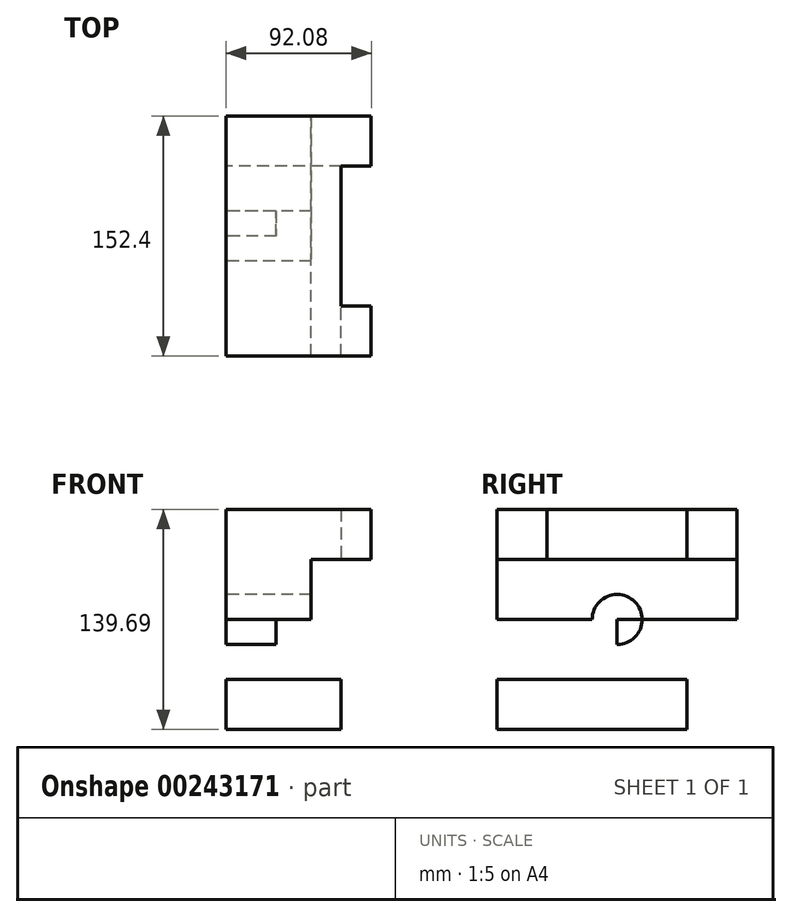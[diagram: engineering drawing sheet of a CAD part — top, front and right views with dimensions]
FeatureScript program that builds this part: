
annotation { "Feature Type Name" : "Feature", "Feature Type Description" : "" }
export const myFeature = defineFeature(function(context is Context, id is Id, definition is map)
    precondition{}
    {
        {
            var Q0;
            Q0=qCreatedBy(makeId("Right.planeOp"),FACE);
            var sketch = newSketch(context, id + "F0", { "sketchPlane" : qUnion([Q0])});
            skLineSegment(sketch, "E0.bottom", {"start": v(-76.2, 85.72) * mm, "end": v(0, 85.72) * mm});
            skLineSegment(sketch, "E0.top", {"start": v(-76.2, -41.28) * mm, "end": v(0, -41.28) * mm});
            skLineSegment(sketch, "E0.left", {"start": v(-76.2, 85.72) * mm, "end": v(-76.2, -41.28) * mm});
            skLineSegment(sketch, "E0.right", {"start": v(0, 85.72) * mm, "end": v(0, -41.28) * mm});
            skLineSegment(sketch, "E1.top", {"start": v(0, 0) * mm, "end": v(-25.4, 0) * mm});
            skLineSegment(sketch, "E1.left", {"start": v(0, -41.28) * mm, "end": v(0, 0) * mm});
            skLineSegment(sketch, "E1.right", {"start": v(-25.4, -41.28) * mm, "end": v(-25.4, 0) * mm});
            skLineSegment(sketch, "E2.top", {"start": v(-76.2, 15.87) * mm, "end": v(0, 15.87) * mm});
            skLineSegment(sketch, "E2.left", {"start": v(-76.2, 85.72) * mm, "end": v(-76.2, 15.87) * mm});
            skLineSegment(sketch, "E2.right", {"start": v(0, 85.72) * mm, "end": v(0, 15.87) * mm});
            skLineSegment(sketch, "E3.top", {"start": v(-76.2, 47.62) * mm, "end": v(0, 47.62) * mm});
            skLineSegment(sketch, "E3.left", {"start": v(-76.2, 85.72) * mm, "end": v(-76.2, 47.62) * mm});
            skLineSegment(sketch, "E3.right", {"start": v(0, 85.72) * mm, "end": v(0, 47.62) * mm});
            skLineSegment(sketch, "E4.left", {"start": v(-76.2, 47.62) * mm, "end": v(-76.2, 15.87) * mm});
            skLineSegment(sketch, "E4.right", {"start": v(0, 47.62) * mm, "end": v(0, 15.87) * mm});
            skLineSegment(sketch, "E5.bottom", {"start": v(-76.2, 47.62) * mm, "end": v(-44.45, 47.62) * mm});
            skLineSegment(sketch, "E5.top", {"start": v(-76.2, 15.87) * mm, "end": v(-44.45, 15.87) * mm});
            skLineSegment(sketch, "E5.right", {"start": v(-44.45, 47.62) * mm, "end": v(-44.45, 15.87) * mm});
            skLineSegment(sketch, "E6.MirrorCS", {"start": v(76.2, 15.87) * mm, "end": v(44.45, 15.87) * mm});
            skLineSegment(sketch, "E7.MirrorCS", {"start": v(76.2, 85.72) * mm, "end": v(76.2, 15.87) * mm});
            skLineSegment(sketch, "E8.MirrorCS", {"start": v(76.2, 47.62) * mm, "end": v(76.2, 15.87) * mm});
            skLineSegment(sketch, "E9.MirrorCS", {"start": v(76.2, 47.62) * mm, "end": v(0, 47.62) * mm});
            skLineSegment(sketch, "E10.MirrorCS", {"start": v(76.2, 85.72) * mm, "end": v(0, 85.72) * mm});
            skLineSegment(sketch, "E11.MirrorCS", {"start": v(76.2, 15.87) * mm, "end": v(0, 15.87) * mm});
            skLineSegment(sketch, "E12.MirrorCS", {"start": v(25.4, -41.28) * mm, "end": v(25.4, 0) * mm});
            skLineSegment(sketch, "E13.MirrorCS", {"start": v(0, 0) * mm, "end": v(25.4, 0) * mm});
            skLineSegment(sketch, "E14.MirrorCS", {"start": v(76.2, 85.72) * mm, "end": v(76.2, -41.28) * mm});
            skLineSegment(sketch, "E15.MirrorCS", {"start": v(76.2, 85.72) * mm, "end": v(76.2, 47.62) * mm});
            skLineSegment(sketch, "E16.MirrorCS", {"start": v(76.2, -41.28) * mm, "end": v(0, -41.28) * mm});
            skLineSegment(sketch, "E17.MirrorCS", {"start": v(44.45, 47.62) * mm, "end": v(44.45, 15.87) * mm});
            skLineSegment(sketch, "E18.MirrorCS", {"start": v(76.2, 47.62) * mm, "end": v(44.45, 47.62) * mm});
            skLineSegment(sketch, "E19", {"start": v(-76.2, 85.72) * mm, "end": v(76.2, 85.72) * mm});
            skLineSegment(sketch, "E20.MirrorCS", {"start": v(76.2, 123.82) * mm, "end": v(76.2, 155.57) * mm});
            skLineSegment(sketch, "E21.MirrorCS", {"start": v(0, 85.72) * mm, "end": v(0, 123.83) * mm});
            skLineSegment(sketch, "E22.MirrorCS", {"start": v(-76.2, 155.58) * mm, "end": v(-44.45, 155.58) * mm});
            skLineSegment(sketch, "E23.MirrorCS", {"start": v(0, 85.72) * mm, "end": v(0, 155.58) * mm});
            skLineSegment(sketch, "E24.MirrorCS", {"start": v(0, 123.82) * mm, "end": v(0, 155.57) * mm});
            skLineSegment(sketch, "E25.MirrorCS", {"start": v(76.2, 85.72) * mm, "end": v(76.2, 155.58) * mm});
            skLineSegment(sketch, "E26.MirrorCS", {"start": v(76.2, 123.83) * mm, "end": v(0, 123.83) * mm});
            skLineSegment(sketch, "E27.MirrorCS", {"start": v(-76.2, 123.83) * mm, "end": v(0, 123.83) * mm});
            skLineSegment(sketch, "E28.MirrorCS", {"start": v(-76.2, 155.58) * mm, "end": v(0, 155.58) * mm});
            skLineSegment(sketch, "E29.MirrorCS", {"start": v(0, 212.72) * mm, "end": v(0, 171.45) * mm});
            skLineSegment(sketch, "E30.MirrorCS", {"start": v(-76.2, 85.72) * mm, "end": v(-76.2, 155.58) * mm});
            skLineSegment(sketch, "E31.MirrorCS", {"start": v(76.2, 85.72) * mm, "end": v(76.2, 123.83) * mm});
            skLineSegment(sketch, "E32.MirrorCS", {"start": v(76.2, 155.58) * mm, "end": v(44.45, 155.58) * mm});
            skLineSegment(sketch, "E33.MirrorCS", {"start": v(-76.2, 123.82) * mm, "end": v(-76.2, 155.57) * mm});
            skLineSegment(sketch, "E34.MirrorCS", {"start": v(76.2, 123.83) * mm, "end": v(44.45, 123.83) * mm});
            skLineSegment(sketch, "E35.MirrorCS", {"start": v(76.2, 155.58) * mm, "end": v(0, 155.58) * mm});
            skLineSegment(sketch, "E36.MirrorCS", {"start": v(76.2, 85.72) * mm, "end": v(76.2, 212.72) * mm});
            skLineSegment(sketch, "E37.MirrorCS", {"start": v(-76.2, 212.72) * mm, "end": v(0, 212.72) * mm});
            skLineSegment(sketch, "E38.MirrorCS", {"start": v(-76.2, 85.72) * mm, "end": v(-76.2, 212.72) * mm});
            skLineSegment(sketch, "E39.MirrorCS", {"start": v(0, 85.72) * mm, "end": v(0, 212.72) * mm});
            skLineSegment(sketch, "E40.MirrorCS", {"start": v(0, 171.45) * mm, "end": v(-25.4, 171.45) * mm});
            skLineSegment(sketch, "E41.MirrorCS", {"start": v(-25.4, 212.72) * mm, "end": v(-25.4, 171.45) * mm});
            skLineSegment(sketch, "E42.MirrorCS", {"start": v(-76.2, 85.72) * mm, "end": v(-76.2, 123.83) * mm});
            skLineSegment(sketch, "E43.MirrorCS", {"start": v(25.4, 212.72) * mm, "end": v(25.4, 171.45) * mm});
            skLineSegment(sketch, "E44.MirrorCS", {"start": v(-44.45, 123.82) * mm, "end": v(-44.45, 155.57) * mm});
            skLineSegment(sketch, "E45.MirrorCS", {"start": v(-76.2, 123.83) * mm, "end": v(-44.45, 123.83) * mm});
            skLineSegment(sketch, "E46.MirrorCS", {"start": v(0, 171.45) * mm, "end": v(25.4, 171.45) * mm});
            skLineSegment(sketch, "E47.MirrorCS", {"start": v(44.45, 123.82) * mm, "end": v(44.45, 155.57) * mm});
            skLineSegment(sketch, "E48.MirrorCS", {"start": v(76.2, 212.72) * mm, "end": v(0, 212.72) * mm});
            skCircle(sketch, "E49", {"center": v(0, 85.72) * mm, "radius": 15.88 * mm});
            skSolve(sketch);
        }
        {
            var Q0;
            {var subQ1=sQuery(id+"F0.wireOp",EDGE,"E38.MirrorCS");Q0=makeQuery(id+"F0.imprint","IMPRINT",FACE,{"disambiguationData":[TD([[makeQuery(id+"F0.imprint","IMPRINT",EDGE,{"derivedFrom":subQ1}),-1.0]])]});}
            var Q1;
            {var subQ1=sQuery(id+"F0.wireOp",EDGE,"E39.MirrorCS");Q1=makeQuery(id+"F0.imprint","IMPRINT",FACE,{"disambiguationData":[TD([[makeQuery(id+"F0.imprint","IMPRINT",EDGE,{"derivedFrom":subQ1}),-1.0]])]});}
            var Q2;
            {var subQ0=sQuery(id+"F0.wireOp",EDGE,"E0.left");Q2=makeQuery(id+"F0.imprint","IMPRINT",FACE,{"disambiguationData":[TD([[makeQuery(id+"F0.imprint","IMPRINT",EDGE,{"derivedFrom":subQ0}),1.0]])]});}
            var Q3;
            {var subQ3=sQuery(id+"F0.wireOp",EDGE,"E0.right");Q3=makeQuery(id+"F0.imprint","IMPRINT",FACE,{"disambiguationData":[TD([[makeQuery(id+"F0.imprint","IMPRINT",EDGE,{"derivedFrom":subQ3}),1.0]])]});}
            extrude(context, id + "F1", {"entities" : qUnion([Q0, Q1, Q2, Q3]), "depth" : 31.75 * mm});
        }
        {
            var Q0;
            {var subQ1=sQuery(id+"F0.wireOp",EDGE,"E27.MirrorCS");Q0=makeQuery(id+"F0.imprint","IMPRINT",FACE,{"disambiguationData":[TD([[makeQuery(id+"F0.imprint","IMPRINT",EDGE,{"derivedFrom":subQ1}),-1.0]])]});}
            var Q1;
            {var subQ0=sQuery(id+"F0.wireOp",EDGE,"E26.MirrorCS");var subQ3=makeQuery(id+"F0.imprint","INTERSECT",VERTEX,{"derivedFrom":[sQuery(id+"F0.wireOp",EDGE,"E47.MirrorCS"),subQ0]});Q1=makeQuery(id+"F0.imprint","IMPRINT",FACE,{"disambiguationData":[TD([[makeQuery(id+"F0.imprint","IMPRINT",EDGE,{"disambiguationData":[TD([[subQ3,1.0]])],"derivedFrom":subQ0}),1.0]])]});}
            var Q2;
            {var subQ0=sQuery(id+"F0.wireOp",EDGE,"E15.MirrorCS");Q2=makeQuery(id+"F0.imprint","IMPRINT",FACE,{"disambiguationData":[TD([[makeQuery(id+"F0.imprint","IMPRINT",EDGE,{"derivedFrom":subQ0}),-1.0]])]});}
            var Q3;
            {var subQ5=sQuery(id+"F0.wireOp",EDGE,"E3.left");Q3=makeQuery(id+"F0.imprint","IMPRINT",FACE,{"disambiguationData":[TD([[makeQuery(id+"F0.imprint","IMPRINT",EDGE,{"derivedFrom":subQ5}),1.0]])]});}
            extrude(context, id + "F2", {"entities" : qUnion([Q0, Q1, Q2, Q3]), "operationType" : NewBodyOperationType.ADD, "depth" : 53.97 * mm});
        }
        {
            var Q0;
            {var subQ4=sQuery(id+"F0.wireOp",EDGE,"E27.MirrorCS");Q0=makeQuery(id+"F0.imprint","IMPRINT",FACE,{"disambiguationData":[TD([[makeQuery(id+"F0.imprint","IMPRINT",EDGE,{"derivedFrom":subQ4}),1.0]])]});}
            var Q1;
            {var subQ5=sQuery(id+"F0.wireOp",EDGE,"E47.MirrorCS");Q1=makeQuery(id+"F0.imprint","IMPRINT",FACE,{"disambiguationData":[TD([[makeQuery(id+"F0.imprint","IMPRINT",EDGE,{"derivedFrom":subQ5}),1.0]])]});}
            var Q2;
            {var subQ0=sQuery(id+"F0.wireOp",EDGE,"E3.top");Q2=makeQuery(id+"F0.imprint","IMPRINT",FACE,{"disambiguationData":[TD([[makeQuery(id+"F0.imprint","IMPRINT",EDGE,{"derivedFrom":subQ0}),-1.0]])]});}
            var Q3;
            {var subQ5=sQuery(id+"F0.wireOp",EDGE,"E17.MirrorCS");Q3=makeQuery(id+"F0.imprint","IMPRINT",FACE,{"disambiguationData":[TD([[makeQuery(id+"F0.imprint","IMPRINT",EDGE,{"derivedFrom":subQ5}),-1.0]])]});}
            extrude(context, id + "F3", {"entities" : qUnion([Q0, Q1, Q2, Q3]), "operationType" : NewBodyOperationType.ADD, "depth" : 73.02 * mm});
        }
        {
            var Q0;
            {var subQ2=sQuery(id+"F0.wireOp",EDGE,"E44.MirrorCS");Q0=makeQuery(id+"F0.imprint","IMPRINT",FACE,{"disambiguationData":[TD([[makeQuery(id+"F0.imprint","IMPRINT",EDGE,{"derivedFrom":subQ2}),1.0]])]});}
            var Q1;
            {var subQ5=sQuery(id+"F0.wireOp",EDGE,"E47.MirrorCS");Q1=makeQuery(id+"F0.imprint","IMPRINT",FACE,{"disambiguationData":[TD([[makeQuery(id+"F0.imprint","IMPRINT",EDGE,{"derivedFrom":subQ5}),-1.0]])]});}
            var Q2;
            Q2=makeQuery(id+"F0.imprint","IMPRINT",FACE,{"disambiguationData":[TD([[makeQuery(id+"F0.imprint","IMPRINT",EDGE,{"derivedFrom":sQuery(id+"F0.wireOp",EDGE,"E5.bottom")}),-1.0]])]});
            var Q3;
            {var subQ0=sQuery(id+"F0.wireOp",EDGE,"E8.MirrorCS");Q3=makeQuery(id+"F0.imprint","IMPRINT",FACE,{"disambiguationData":[TD([[makeQuery(id+"F0.imprint","IMPRINT",EDGE,{"derivedFrom":subQ0}),-1.0]])]});}
            extrude(context, id + "F4", {"entities" : qUnion([Q0, Q1, Q2, Q3]), "operationType" : NewBodyOperationType.ADD, "depth" : 92.07 * mm});
        }
    });
